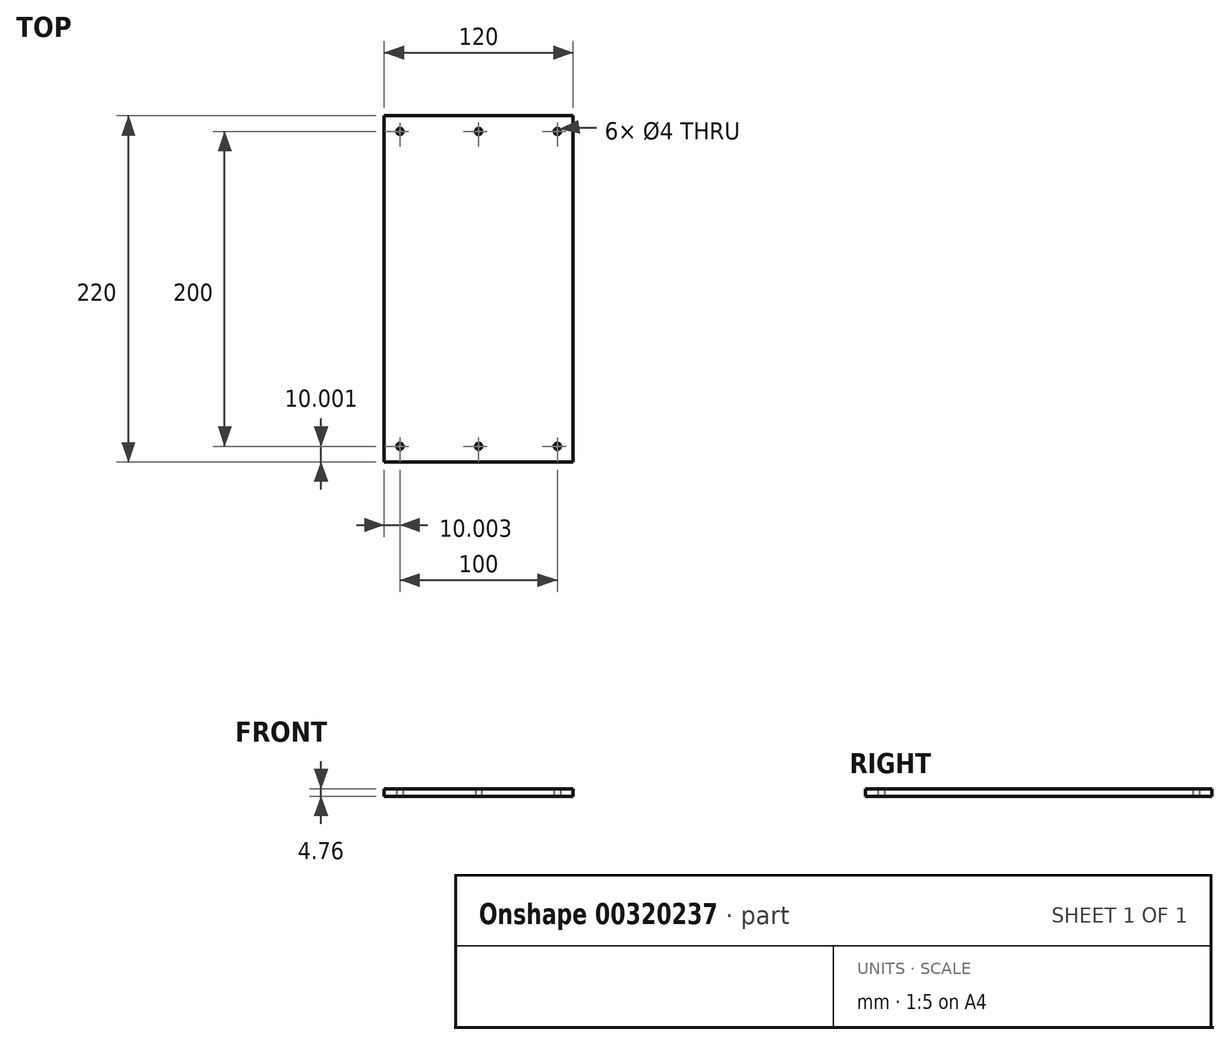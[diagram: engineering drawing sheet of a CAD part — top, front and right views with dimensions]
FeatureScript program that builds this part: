
annotation { "Feature Type Name" : "Feature", "Feature Type Description" : "" }
export const myFeature = defineFeature(function(context is Context, id is Id, definition is map)
    precondition{}
    {
        {
            var Q0;
            Q0=qCreatedBy(makeId("Top.planeOp"),FACE);
            var sketch = newSketch(context, id + "F0", { "sketchPlane" : qUnion([Q0])});
            skLineSegment(sketch, "E0.bottom", {"start": v(-47.43, 50.1) * mm, "end": v(72.57, 50.1) * mm});
            skLineSegment(sketch, "E0.top", {"start": v(-47.43, -169.9) * mm, "end": v(72.57, -169.9) * mm});
            skLineSegment(sketch, "E0.left", {"start": v(-47.43, 50.1) * mm, "end": v(-47.43, -169.9) * mm});
            skLineSegment(sketch, "E0.right", {"start": v(72.57, 50.1) * mm, "end": v(72.57, -169.9) * mm});
            skCircle(sketch, "E1", {"center": v(-37.43, 40.1) * mm, "radius": 2 * mm});
            skCircle(sketch, "E2.0.1.0", {"center": v(-37.43, -159.9) * mm, "radius": 2 * mm});
            skCircle(sketch, "E2.1.0.0", {"center": v(12.57, 40.1) * mm, "radius": 2 * mm});
            skCircle(sketch, "E2.1.1.0", {"center": v(12.57, -159.9) * mm, "radius": 2 * mm});
            skCircle(sketch, "E2.2.0.0", {"center": v(62.57, 40.1) * mm, "radius": 2 * mm});
            skCircle(sketch, "E2.2.1.0", {"center": v(62.57, -159.9) * mm, "radius": 2 * mm});
            skLineSegment(sketch, "E2.direction1", {"start": v(-37.43, 40.1) * mm, "end": v(12.57, 40.1) * mm, "construction": true});
            skLineSegment(sketch, "E2.direction2", {"start": v(-37.43, 40.1) * mm, "end": v(-37.43, -159.9) * mm, "construction": true});
            skSolve(sketch);
        }
        {
            var Q0;
            Q0 = qSketchRegion(id + "F0", true);
            extrude(context, id + "F1", {"entities" : qUnion([Q0]), "depth" : 4.76 * mm});
        }
    });
